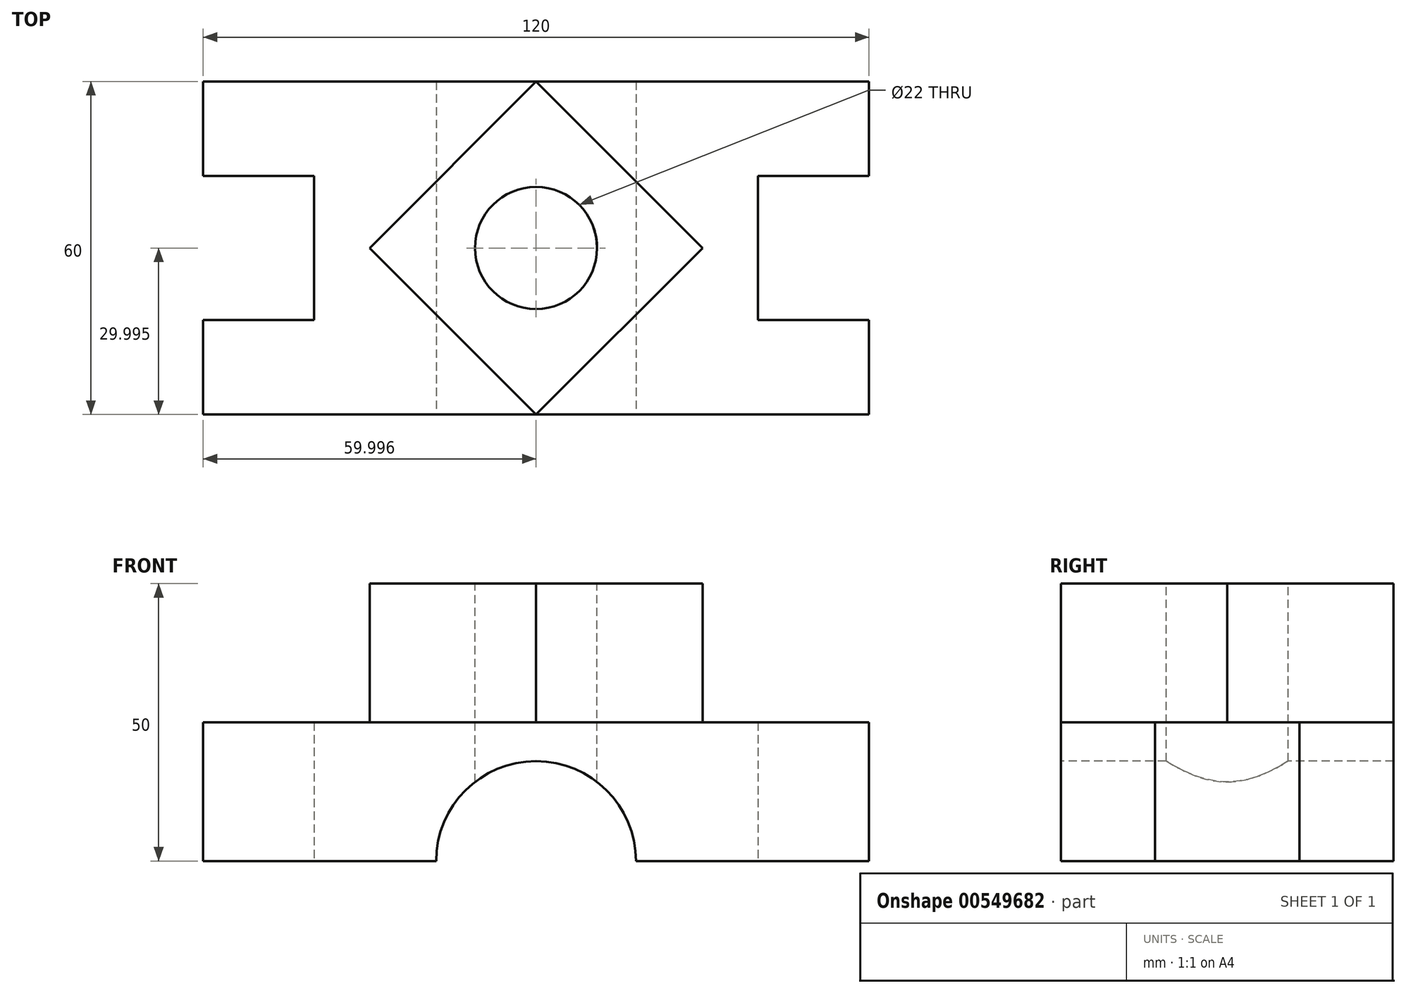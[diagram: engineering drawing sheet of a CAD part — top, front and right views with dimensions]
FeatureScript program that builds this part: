
annotation { "Feature Type Name" : "Feature", "Feature Type Description" : "" }
export const myFeature = defineFeature(function(context is Context, id is Id, definition is map)
    precondition{}
    {
        {
            var Q0;
            Q0=qCreatedBy(makeId("Top.planeOp"),FACE);
            var sketch = newSketch(context, id + "F0", { "sketchPlane" : qUnion([Q0])});
            skLineSegment(sketch, "E0.bottom", {"start": v(28.86, -17.84) * mm, "end": v(-91.14, -17.84) * mm});
            skLineSegment(sketch, "E0.top", {"start": v(28.86, 42.16) * mm, "end": v(-91.14, 42.16) * mm});
            skLineSegment(sketch, "E0.left", {"start": v(28.86, -17.84) * mm, "end": v(28.86, -0.84) * mm});
            skLineSegment(sketch, "E0.right", {"start": v(-91.14, -17.84) * mm, "end": v(-91.14, -0.84) * mm});
            skPoint(sketch, "E0.middle", {"position": v(-31.14, 12.16) * mm});
            skLineSegment(sketch, "E1.bottom", {"start": v(28.86, 25.16) * mm, "end": v(8.86, 25.16) * mm});
            skLineSegment(sketch, "E1.top", {"start": v(28.86, -0.84) * mm, "end": v(8.86, -0.84) * mm});
            skLineSegment(sketch, "E1.right", {"start": v(8.86, 25.16) * mm, "end": v(8.86, -0.84) * mm});
            skPoint(sketch, "E1.middle", {"position": v(28.86, 12.16) * mm});
            skLineSegment(sketch, "E2.bottom", {"start": v(-91.14, 25.16) * mm, "end": v(-71.14, 25.16) * mm});
            skLineSegment(sketch, "E2.top", {"start": v(-91.14, -0.84) * mm, "end": v(-71.14, -0.84) * mm});
            skLineSegment(sketch, "E2.right", {"start": v(-71.14, 25.16) * mm, "end": v(-71.14, -0.84) * mm});
            skPoint(sketch, "E2.middle", {"position": v(-91.14, 12.16) * mm});
            skPoint(sketch, "E3.orphan", {"position": v(-111.14, 25.16) * mm});
            skPoint(sketch, "E4.orphan", {"position": v(-111.14, -0.84) * mm});
            skLineSegment(sketch, "E5.trimOffspring", {"start": v(-91.14, 25.16) * mm, "end": v(-91.14, 42.16) * mm});
            skPoint(sketch, "E1.left.start.orphan", {"position": v(48.86, 25.16) * mm});
            skPoint(sketch, "E6.orphan", {"position": v(48.86, -0.84) * mm});
            skLineSegment(sketch, "E7.trimOffspring", {"start": v(28.86, 25.16) * mm, "end": v(28.86, 42.16) * mm});
            skSolve(sketch);
        }
        {
            var Q0;
            Q0 = qSketchRegion(id + "F0", true);
            extrude(context, id + "F1", {"entities" : qUnion([Q0]), "depth" : 25 * mm, "offsetDistance" : 25 * mm});
        }
        {
            var Q0;
            Q0=makeQuery(id+"F1.opExtrude","CAP_FACE",FACE,{"disambiguationData":[OSD([sQuery(id+"F0.wireOp",EDGE,"E0.bottom"),sQuery(id+"F0.wireOp",EDGE,"E0.top"),sQuery(id+"F0.wireOp",EDGE,"E0.left"),sQuery(id+"F0.wireOp",EDGE,"E0.right"),sQuery(id+"F0.wireOp",EDGE,"E1.bottom"),sQuery(id+"F0.wireOp",EDGE,"E1.top"),sQuery(id+"F0.wireOp",EDGE,"E1.right"),sQuery(id+"F0.wireOp",EDGE,"E2.bottom"),sQuery(id+"F0.wireOp",EDGE,"E2.top"),sQuery(id+"F0.wireOp",EDGE,"E2.right"),sQuery(id+"F0.wireOp",EDGE,"E5.trimOffspring"),sQuery(id+"F0.wireOp",EDGE,"E7.trimOffspring")])],"isStart":false});
            var sketch = newSketch(context, id + "F2", { "sketchPlane" : qUnion([Q0])});
            skLineSegment(sketch, "E8", {"start": v(-31.14, 42.16) * mm, "end": v(-61.14, 12.16) * mm});
            skLineSegment(sketch, "E9", {"start": v(-61.14, 12.16) * mm, "end": v(-31.14, -17.84) * mm});
            skLineSegment(sketch, "E10", {"start": v(-31.14, -17.84) * mm, "end": v(-1.14, 12.16) * mm});
            skLineSegment(sketch, "E11", {"start": v(-1.14, 12.16) * mm, "end": v(-31.14, 42.16) * mm});
            skSolve(sketch);
        }
        {
            var Q0;
            Q0=makeQuery(id+"F2.imprint","IMPRINT",FACE,{"disambiguationData":[TD([[makeQuery(id+"F2.imprint","IMPRINT",EDGE,{"derivedFrom":sQuery(id+"F2.wireOp",EDGE,"E8")}),1.0]])]});
            extrude(context, id + "F3", {"entities" : qUnion([Q0]), "operationType" : NewBodyOperationType.ADD, "depth" : 25 * mm, "offsetDistance" : 25 * mm});
        }
        {
            var Q0;
            Q0=makeQuery(id+"F1.opExtrude","SWEPT_FACE",FACE,{"disambiguationData":[OSD([sQuery(id+"F0.wireOp",EDGE,"E0.bottom")])]});
            var sketch = newSketch(context, id + "F4", { "sketchPlane" : qUnion([Q0])});
            skCircle(sketch, "E12", {"center": v(-31.14, 0) * mm, "radius": 18 * mm});
            skSolve(sketch);
        }
        {
            var Q0;
            Q0 = qSketchRegion(id + "F4", true);
            extrude(context, id + "F5", {"entities" : qUnion([Q0]), "operationType" : NewBodyOperationType.REMOVE, "endBound" : BoundingType.THROUGH_ALL, "oppositeDirection" : true, "depth" : 25 * mm, "offsetDistance" : 25 * mm});
        }
        {
            var Q0;
            Q0=makeQuery(id+"F3.opExtrude","CAP_FACE",FACE,{"disambiguationData":[OSD([sQuery(id+"F2.wireOp",EDGE,"E8"),sQuery(id+"F2.wireOp",EDGE,"E9"),sQuery(id+"F2.wireOp",EDGE,"E10"),sQuery(id+"F2.wireOp",EDGE,"E11")])],"isStart":false});
            var sketch = newSketch(context, id + "F6", { "sketchPlane" : qUnion([Q0])});
            skCircle(sketch, "E13", {"center": v(-31.14, 12.16) * mm, "radius": 11 * mm});
            skSolve(sketch);
        }
        {
            var Q0;
            Q0=makeQuery(id+"F6.imprint","IMPRINT",FACE,{"disambiguationData":[TD([[makeQuery(id+"F6.imprint","IMPRINT",EDGE,{"derivedFrom":sQuery(id+"F6.wireOp",EDGE,"E13")}),1.0]])]});
            extrude(context, id + "F7", {"entities" : qUnion([Q0]), "operationType" : NewBodyOperationType.REMOVE, "endBound" : BoundingType.THROUGH_ALL, "oppositeDirection" : true, "depth" : 25 * mm, "offsetDistance" : 25 * mm});
        }
    });
